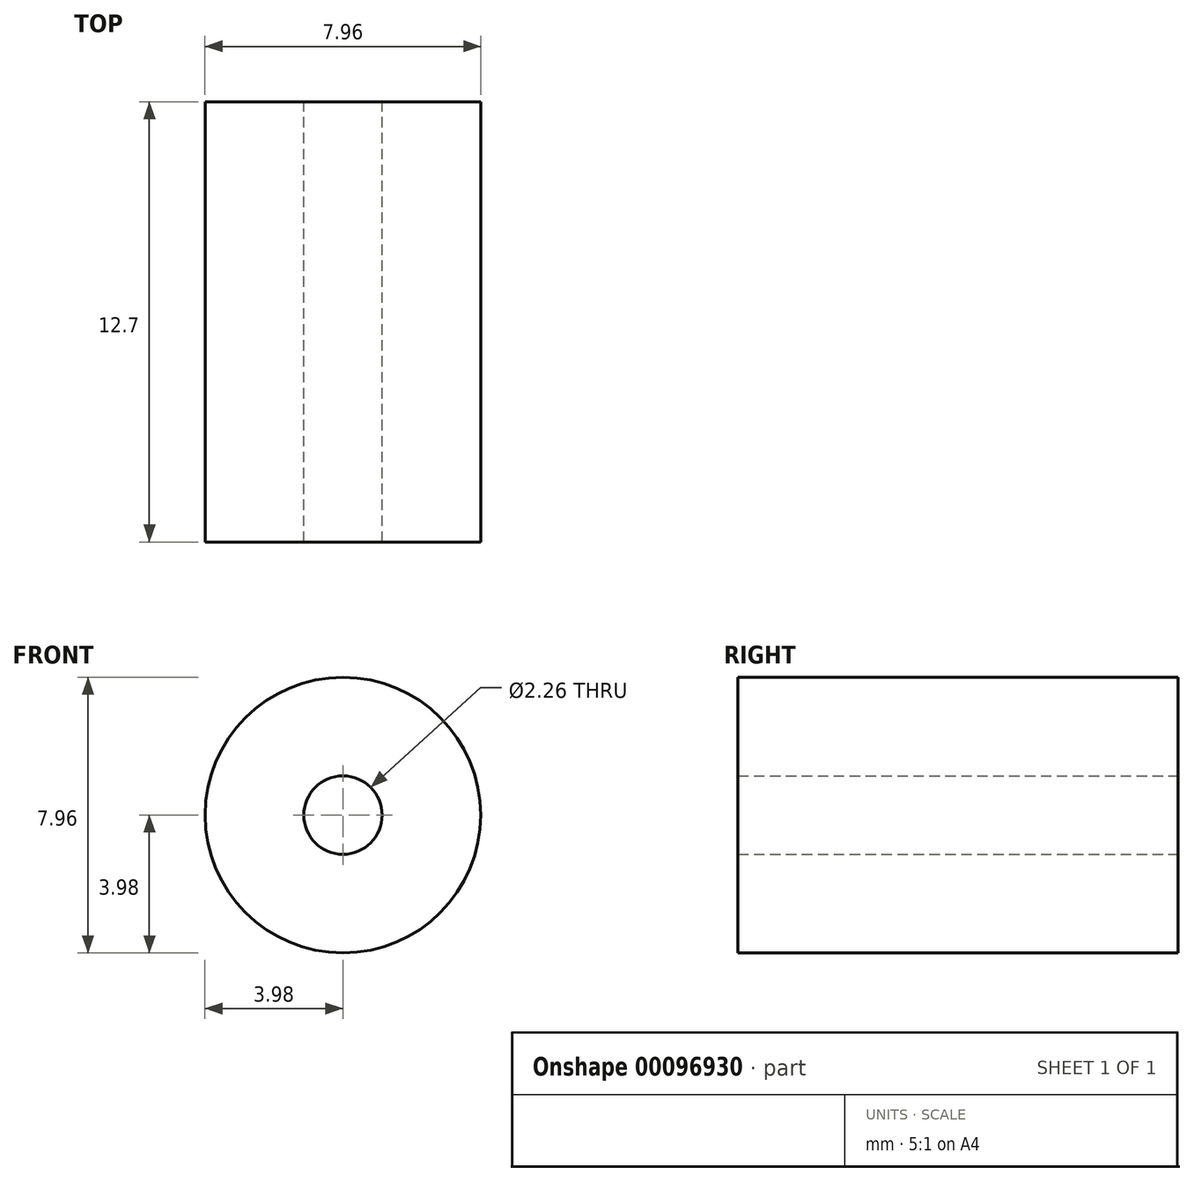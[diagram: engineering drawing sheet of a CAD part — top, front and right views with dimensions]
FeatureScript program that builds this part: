
annotation { "Feature Type Name" : "Feature", "Feature Type Description" : "" }
export const myFeature = defineFeature(function(context is Context, id is Id, definition is map)
    precondition{}
    {
        {
            var Q0;
            Q0=qCreatedBy(makeId("Front.planeOp"),FACE);
            var sketch = newSketch(context, id + "F0", { "sketchPlane" : qUnion([Q0])});
            skCircle(sketch, "E0", {"center": v(0, 0) * mm, "radius": 3.98 * mm});
            skCircle(sketch, "E1", {"center": v(0, 0) * mm, "radius": 1.13 * mm});
            skSolve(sketch);
        }
        {
            var Q0;
            Q0=makeQuery(id+"F0.imprint","IMPRINT",FACE,{"disambiguationData":[TD([[makeQuery(id+"F0.imprint","IMPRINT",EDGE,{"derivedFrom":sQuery(id+"F0.wireOp",EDGE,"E0")}),1.0]])]});
            extrude(context, id + "F1", {"entities" : qUnion([Q0]), "depth" : 12.7 * mm});
        }
    });
